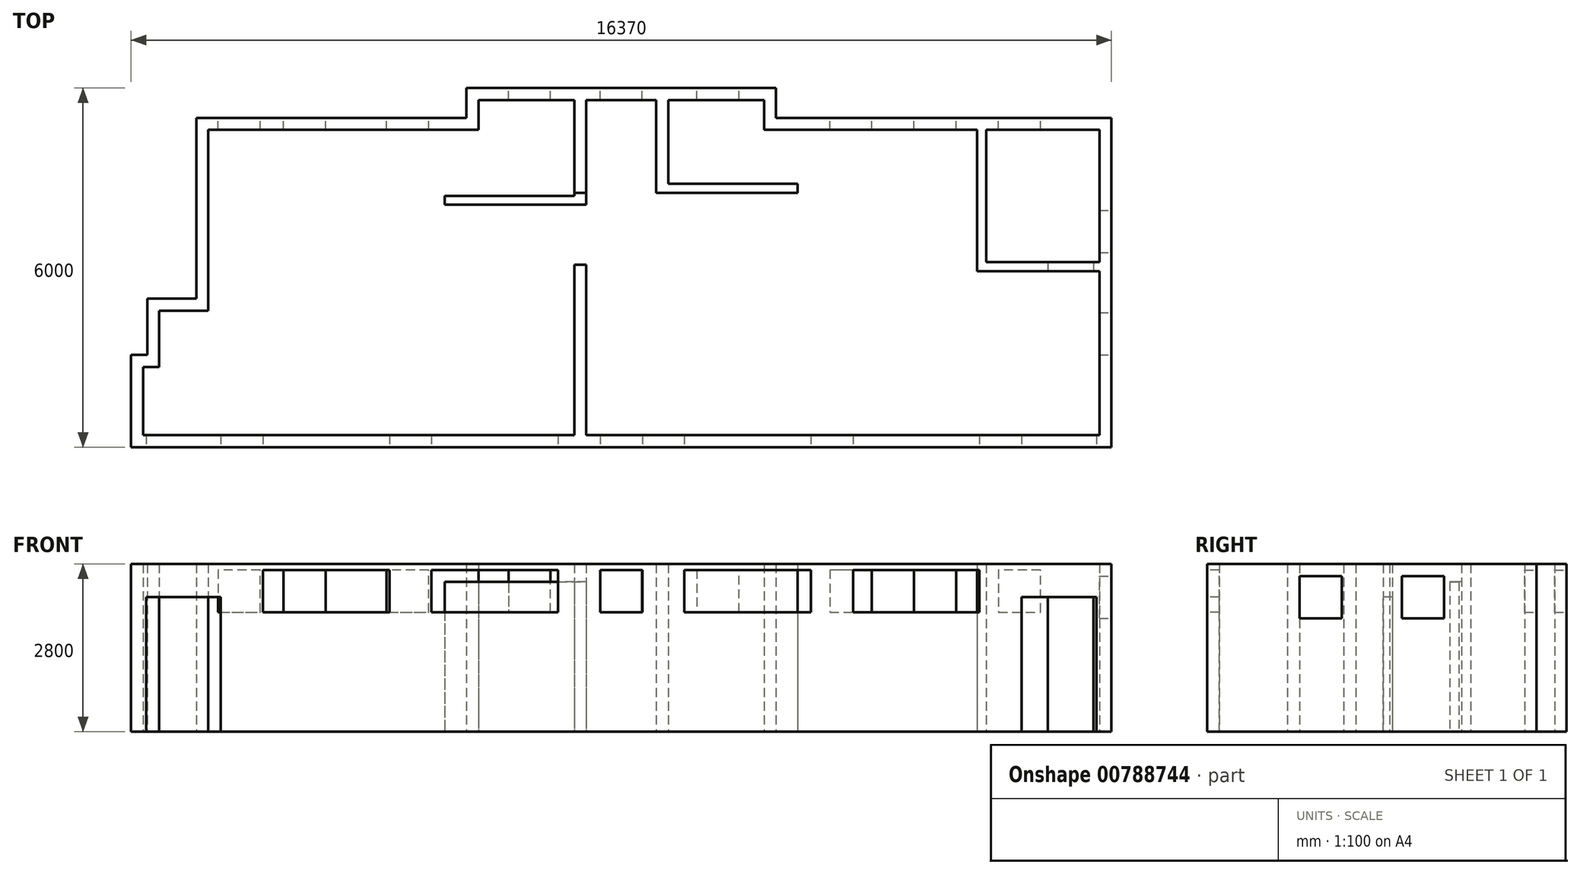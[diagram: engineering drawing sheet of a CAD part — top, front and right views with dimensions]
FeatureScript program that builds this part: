
annotation { "Feature Type Name" : "Feature", "Feature Type Description" : "" }
export const myFeature = defineFeature(function(context is Context, id is Id, definition is map)
    precondition{}
    {
        {
            var Q0;
            Q0=qCreatedBy(makeId("Top.planeOp"),FACE);
            var sketch = newSketch(context, id + "F0", { "sketchPlane" : qUnion([Q0])});
            skLineSegment(sketch, "E0", {"start": v(5800, 5300) * mm, "end": v(5800, 5800) * mm});
            skLineSegment(sketch, "E1", {"start": v(0, 0) * mm, "end": v(16370, 0) * mm});
            skLineSegment(sketch, "E2", {"start": v(16370, 0) * mm, "end": v(16370, 5500) * mm});
            skLineSegment(sketch, "E3", {"start": v(16370, 5500) * mm, "end": v(10770, 5500) * mm});
            skLineSegment(sketch, "E4", {"start": v(10770, 5500) * mm, "end": v(10770, 6000) * mm});
            skLineSegment(sketch, "E5", {"start": v(10770, 6000) * mm, "end": v(5600, 6000) * mm});
            skLineSegment(sketch, "E6", {"start": v(5600, 6000) * mm, "end": v(5600, 5500) * mm});
            skLineSegment(sketch, "E7", {"start": v(10570, 5800) * mm, "end": v(10570, 5300) * mm});
            skLineSegment(sketch, "E8", {"start": v(10570, 5300) * mm, "end": v(16170, 5300) * mm});
            skLineSegment(sketch, "E9", {"start": v(16170, 5300) * mm, "end": v(16170, 200) * mm});
            skLineSegment(sketch, "E10", {"start": v(0, 200) * mm, "end": v(0, 0) * mm});
            skLineSegment(sketch, "E11", {"start": v(0, 0) * mm, "end": v(0, 1540) * mm});
            skPoint(sketch, "E11.endSnap0", {"position": v(0, 100) * mm});
            skLineSegment(sketch, "E12", {"start": v(16170, 200) * mm, "end": v(200, 200) * mm});
            skLineSegment(sketch, "E13", {"start": v(200, 200) * mm, "end": v(200, 1340) * mm});
            skLineSegment(sketch, "E14", {"start": v(200, 1340) * mm, "end": v(470, 1340) * mm});
            skLineSegment(sketch, "E15", {"start": v(0, 1540) * mm, "end": v(270, 1540) * mm});
            skLineSegment(sketch, "E16", {"start": v(270, 1540) * mm, "end": v(270, 2480) * mm});
            skLineSegment(sketch, "E17", {"start": v(470, 1340) * mm, "end": v(470, 2280) * mm});
            skLineSegment(sketch, "E18", {"start": v(470, 2280) * mm, "end": v(936.4, 2280) * mm});
            skLineSegment(sketch, "E19", {"start": v(270, 2480) * mm, "end": v(1090, 2480) * mm});
            skLineSegment(sketch, "E20", {"start": v(5600, 5500) * mm, "end": v(1090, 5500) * mm});
            skLineSegment(sketch, "E21", {"start": v(5800, 5300) * mm, "end": v(1290, 5300) * mm});
            skLineSegment(sketch, "E22", {"start": v(1290, 5300) * mm, "end": v(1290, 2280) * mm});
            skLineSegment(sketch, "E23", {"start": v(1290, 2280) * mm, "end": v(936.4, 2280) * mm});
            skLineSegment(sketch, "E24", {"start": v(1090, 2480) * mm, "end": v(1090, 5500) * mm});
            skLineSegment(sketch, "E25", {"start": v(10570, 5800) * mm, "end": v(5800, 5800) * mm});
            skLineSegment(sketch, "E26", {"start": v(1090, 5500) * mm, "end": v(1090, 5300) * mm});
            skLineSegment(sketch, "E27", {"start": v(1090, 5500) * mm, "end": v(0, 5500) * mm});
            skLineSegment(sketch, "E28", {"start": v(0, 5500) * mm, "end": v(0, 5042) * mm});
            skLineSegment(sketch, "E29", {"start": v(0, 5042) * mm, "end": v(458, 5042) * mm});
            skLineSegment(sketch, "E30", {"start": v(458, 5042) * mm, "end": v(458, 5300) * mm});
            skLineSegment(sketch, "E31", {"start": v(458, 5300) * mm, "end": v(1090, 5300) * mm});
            skSolve(sketch);
        }
        {
            var Q0;
            {var subQ2=sQuery(id+"F0.wireOp",EDGE,"E1");Q0=makeQuery(id+"F0.imprint","IMPRINT",FACE,{"disambiguationData":[TD([[makeQuery(id+"F0.imprint","IMPRINT",EDGE,{"derivedFrom":subQ2}),1.0]])]});}
            extrude(context, id + "F1", {"entities" : qUnion([Q0]), "depth" : 2800 * mm, "offsetDistance" : 25 * mm});
        }
        {
            var Q0;
            Q0=makeQuery(id+"F1.opExtrude","SWEPT_FACE",FACE,{"disambiguationData":[OSD([sQuery(id+"F0.wireOp",EDGE,"E1")])]});
            var sketch = newSketch(context, id + "F2", { "sketchPlane" : qUnion([Q0])});
            skLineSegment(sketch, "E32", {"start": v(250, 0) * mm, "end": v(250, 2250) * mm});
            skLineSegment(sketch, "E33", {"start": v(250, 2250) * mm, "end": v(1500, 2250) * mm});
            skLineSegment(sketch, "E34", {"start": v(1500, 2250) * mm, "end": v(1500, 0) * mm});
            skLineSegment(sketch, "E35", {"start": v(1500, 0) * mm, "end": v(250, 0) * mm});
            skSolve(sketch);
        }
        {
            var Q0;
            Q0=makeQuery(id+"F2.imprint","IMPRINT",FACE,{"disambiguationData":[TD([[makeQuery(id+"F2.imprint","IMPRINT",EDGE,{"derivedFrom":sQuery(id+"F2.wireOp",EDGE,"E32")}),-1.0]])]});
            extrude(context, id + "F3", {"entities" : qUnion([Q0]), "operationType" : NewBodyOperationType.REMOVE, "oppositeDirection" : true, "depth" : 200 * mm, "offsetDistance" : 25 * mm});
        }
        {
            var Q0;
            Q0=makeQuery(id+"F1.opExtrude","SWEPT_FACE",FACE,{"disambiguationData":[OSD([sQuery(id+"F0.wireOp",EDGE,"E1")])]});
            var sketch = newSketch(context, id + "F4", { "sketchPlane" : qUnion([Q0])});
            skLineSegment(sketch, "E36", {"start": v(16120, 0) * mm, "end": v(16120, 2250) * mm});
            skLineSegment(sketch, "E37", {"start": v(16120, 2250) * mm, "end": v(14870, 2250) * mm});
            skLineSegment(sketch, "E38", {"start": v(14870, 2250) * mm, "end": v(14870, 0) * mm});
            skLineSegment(sketch, "E39", {"start": v(14870, 0) * mm, "end": v(16120, 0) * mm});
            skSolve(sketch);
        }
        {
            var Q0;
            Q0=makeQuery(id+"F4.imprint","IMPRINT",FACE,{"disambiguationData":[TD([[makeQuery(id+"F4.imprint","IMPRINT",EDGE,{"derivedFrom":sQuery(id+"F4.wireOp",EDGE,"E36")}),1.0]])]});
            extrude(context, id + "F5", {"entities" : qUnion([Q0]), "operationType" : NewBodyOperationType.REMOVE, "oppositeDirection" : true, "depth" : 200 * mm, "offsetDistance" : 25 * mm});
        }
        {
            var Q0;
            Q0=qCreatedBy(makeId("Top.planeOp"),FACE);
            var sketch = newSketch(context, id + "F6", { "sketchPlane" : qUnion([Q0])});
            skLineSegment(sketch, "E40", {"start": v(1290, 2280) * mm, "end": v(3550, 2280) * mm});
            skLineSegment(sketch, "E41", {"start": v(3550, 2280) * mm, "end": v(3550, 5300) * mm});
            skLineSegment(sketch, "E42", {"start": v(3550, 5300) * mm, "end": v(3350, 5300) * mm});
            skLineSegment(sketch, "E43", {"start": v(3350, 2480) * mm, "end": v(1290, 2480) * mm});
            skLineSegment(sketch, "E44", {"start": v(1290, 2480) * mm, "end": v(1290, 2280) * mm});
            skLineSegment(sketch, "E45", {"start": v(3350, 5300) * mm, "end": v(3350, 2480) * mm});
            skSolve(sketch);
        }
        {
            var Q0;
            Q0=qCreatedBy(makeId("Top.planeOp"),FACE);
            var sketch = newSketch(context, id + "F7", { "sketchPlane" : qUnion([Q0])});
            skLineSegment(sketch, "E46.0", {"start": v(5800, 5300) * mm, "end": v(5800, 5800) * mm});
            skLineSegment(sketch, "E47.0", {"start": v(10570, 5800) * mm, "end": v(5800, 5800) * mm});
            skLineSegment(sketch, "E48.0", {"start": v(16170, 200) * mm, "end": v(200, 200) * mm});
            skLineSegment(sketch, "E49", {"start": v(5800, 5800) * mm, "end": v(7400, 5800) * mm});
            skLineSegment(sketch, "E50", {"start": v(7400, 5800) * mm, "end": v(7600, 5800) * mm});
            skLineSegment(sketch, "E51", {"start": v(7600, 5800) * mm, "end": v(7600, 200) * mm});
            skLineSegment(sketch, "E52", {"start": v(7400, 5800) * mm, "end": v(7400, 200) * mm});
            skSolve(sketch);
        }
        {
            var Q0;
            Q0=qCreatedBy(makeId("Top.planeOp"),FACE);
            var sketch = newSketch(context, id + "F8", { "sketchPlane" : qUnion([Q0])});
            skLineSegment(sketch, "E53.0", {"start": v(10570, 5800) * mm, "end": v(10570, 5300) * mm});
            skLineSegment(sketch, "E53.1", {"start": v(10570, 5800) * mm, "end": v(5800, 5800) * mm});
            skLineSegment(sketch, "E53.2", {"start": v(16170, 200) * mm, "end": v(200, 200) * mm});
            skLineSegment(sketch, "E54", {"start": v(8970, 200) * mm, "end": v(8770, 200) * mm});
            skLineSegment(sketch, "E55", {"start": v(8770, 200) * mm, "end": v(8770, 5800) * mm});
            skLineSegment(sketch, "E56", {"start": v(8770, 5800) * mm, "end": v(8970, 5800) * mm});
            skLineSegment(sketch, "E57", {"start": v(8970, 5800) * mm, "end": v(8970, 200) * mm});
            skSolve(sketch);
        }
        {
            var Q0;
            Q0=qCreatedBy(makeId("Top.planeOp"),FACE);
            var sketch = newSketch(context, id + "F9", { "sketchPlane" : qUnion([Q0])});
            skLineSegment(sketch, "E58.0", {"start": v(10570, 5800) * mm, "end": v(5800, 5800) * mm});
            skLineSegment(sketch, "E58.1", {"start": v(10570, 5800) * mm, "end": v(10570, 5300) * mm});
            skLineSegment(sketch, "E59", {"start": v(10570, 5800) * mm, "end": v(8969, 5800) * mm});
            skLineSegment(sketch, "E60", {"start": v(8969, 5800) * mm, "end": v(8969, 4400) * mm});
            skLineSegment(sketch, "E61", {"start": v(8969, 4400) * mm, "end": v(11129, 4400) * mm});
            skLineSegment(sketch, "E62", {"start": v(11129, 4400) * mm, "end": v(11129, 4250) * mm});
            skLineSegment(sketch, "E63", {"start": v(11129, 4250) * mm, "end": v(8769, 4250) * mm});
            skLineSegment(sketch, "E64", {"start": v(8769, 4250) * mm, "end": v(8769, 5800) * mm});
            skSolve(sketch);
        }
        {
            var Q0;
            Q0=qCreatedBy(makeId("Top.planeOp"),FACE);
            var sketch = newSketch(context, id + "F10", { "sketchPlane" : qUnion([Q0])});
            skLineSegment(sketch, "E65", {"start": v(7400, 5800) * mm, "end": v(7400, 4200) * mm});
            skLineSegment(sketch, "E66", {"start": v(7400, 4200) * mm, "end": v(5240, 4200) * mm});
            skLineSegment(sketch, "E67", {"start": v(5240, 4200) * mm, "end": v(5240, 4050) * mm});
            skLineSegment(sketch, "E68", {"start": v(5240, 4050) * mm, "end": v(7600, 4050) * mm});
            skLineSegment(sketch, "E69", {"start": v(7600, 4050) * mm, "end": v(7600, 5800) * mm});
            skLineSegment(sketch, "E70", {"start": v(7400, 5800) * mm, "end": v(7600, 5800) * mm});
            skSolve(sketch);
        }
        {
            var Q0;
            Q0=qSketchRegion(id+"F10",true);
            extrude(context, id + "F11", {"entities" : qUnion([Q0]), "operationType" : NewBodyOperationType.ADD, "depth" : 2500 * mm, "offsetDistance" : 25 * mm});
        }
        {
            var Q0;
            Q0=qCreatedBy(makeId("Top.planeOp"),FACE);
            var sketch = newSketch(context, id + "F12", { "sketchPlane" : qUnion([Q0])});
            skLineSegment(sketch, "E71.0", {"start": v(10570, 5300) * mm, "end": v(16170, 5300) * mm});
            skLineSegment(sketch, "E71.1", {"start": v(16170, 5300) * mm, "end": v(16170, 200) * mm});
            skLineSegment(sketch, "E72", {"start": v(16170, 5300) * mm, "end": v(16170, 3090) * mm});
            skLineSegment(sketch, "E73", {"start": v(16170, 3090) * mm, "end": v(14280, 3090) * mm});
            skLineSegment(sketch, "E74", {"start": v(14280, 3090) * mm, "end": v(14280, 5300) * mm});
            skLineSegment(sketch, "E75", {"start": v(14280, 5300) * mm, "end": v(14130, 5300) * mm});
            skLineSegment(sketch, "E76", {"start": v(14130, 5300) * mm, "end": v(14130, 2940) * mm});
            skLineSegment(sketch, "E77", {"start": v(14130, 2940) * mm, "end": v(16170, 2940) * mm});
            skSolve(sketch);
        }
        {
            var Q0;
            {var subQ0=sQuery(id+"F12.wireOp",EDGE,"E73");Q0=makeQuery(id+"F12.imprint","IMPRINT",FACE,{"disambiguationData":[TD([[makeQuery(id+"F12.imprint","IMPRINT",EDGE,{"derivedFrom":subQ0}),1.0]])]});}
            extrude(context, id + "F13", {"entities" : qUnion([Q0]), "operationType" : NewBodyOperationType.ADD, "depth" : 2800 * mm, "offsetDistance" : 25 * mm});
        }
        {
            var Q0;
            Q0=makeQuery(id+"F1.opExtrude","SWEPT_FACE",FACE,{"disambiguationData":[OSD([sQuery(id+"F0.wireOp",EDGE,"E1")])]});
            var sketch = newSketch(context, id + "F14", { "sketchPlane" : qUnion([Q0])});
            skLineSegment(sketch, "E78", {"start": v(2204, 1996) * mm, "end": v(2204, 2700) * mm});
            skLineSegment(sketch, "E79", {"start": v(2204, 2700) * mm, "end": v(4315, 2700) * mm});
            skLineSegment(sketch, "E80", {"start": v(4315, 2700) * mm, "end": v(4315, 1996) * mm});
            skLineSegment(sketch, "E81", {"start": v(4315, 1996) * mm, "end": v(2204, 1996) * mm});
            skLineSegment(sketch, "E82", {"start": v(5018, 1996) * mm, "end": v(5018, 2700) * mm});
            skLineSegment(sketch, "E83", {"start": v(5018, 2700) * mm, "end": v(7129, 2700) * mm});
            skLineSegment(sketch, "E84", {"start": v(7129, 2700) * mm, "end": v(7129, 1996) * mm});
            skLineSegment(sketch, "E85", {"start": v(7129, 1996) * mm, "end": v(5018, 1996) * mm});
            skLineSegment(sketch, "E86", {"start": v(7833, 1996) * mm, "end": v(7833, 2700) * mm});
            skLineSegment(sketch, "E87", {"start": v(7833, 2700) * mm, "end": v(8537, 2700) * mm});
            skLineSegment(sketch, "E88", {"start": v(8537, 2700) * mm, "end": v(8537, 1996) * mm});
            skLineSegment(sketch, "E89", {"start": v(8537, 1996) * mm, "end": v(7833, 1996) * mm});
            skLineSegment(sketch, "E90", {"start": v(9241, 1996) * mm, "end": v(9241, 2700) * mm});
            skLineSegment(sketch, "E91", {"start": v(9241, 2700) * mm, "end": v(11352, 2700) * mm});
            skLineSegment(sketch, "E92", {"start": v(11352, 2700) * mm, "end": v(11352, 1996) * mm});
            skLineSegment(sketch, "E93", {"start": v(11352, 1996) * mm, "end": v(9241, 1996) * mm});
            skLineSegment(sketch, "E94", {"start": v(12056, 1996) * mm, "end": v(12056, 2700) * mm});
            skLineSegment(sketch, "E95", {"start": v(12056, 2700) * mm, "end": v(14167, 2700) * mm});
            skLineSegment(sketch, "E96", {"start": v(14167, 2700) * mm, "end": v(14167, 1996) * mm});
            skLineSegment(sketch, "E97", {"start": v(14167, 1996) * mm, "end": v(12056, 1996) * mm});
            skSolve(sketch);
        }
        {
            var Q0;
            Q0=makeQuery(id+"F14.imprint","IMPRINT",FACE,{"disambiguationData":[TD([[makeQuery(id+"F14.imprint","IMPRINT",EDGE,{"derivedFrom":sQuery(id+"F14.wireOp",EDGE,"E78")}),-1.0]])]});
            var Q1;
            Q1=makeQuery(id+"F14.imprint","IMPRINT",FACE,{"disambiguationData":[TD([[makeQuery(id+"F14.imprint","IMPRINT",EDGE,{"derivedFrom":sQuery(id+"F14.wireOp",EDGE,"E82")}),-1.0]])]});
            var Q2;
            Q2=makeQuery(id+"F14.imprint","IMPRINT",FACE,{"disambiguationData":[TD([[makeQuery(id+"F14.imprint","IMPRINT",EDGE,{"derivedFrom":sQuery(id+"F14.wireOp",EDGE,"E86")}),-1.0]])]});
            var Q3;
            Q3=makeQuery(id+"F14.imprint","IMPRINT",FACE,{"disambiguationData":[TD([[makeQuery(id+"F14.imprint","IMPRINT",EDGE,{"derivedFrom":sQuery(id+"F14.wireOp",EDGE,"E90")}),-1.0]])]});
            var Q4;
            Q4=makeQuery(id+"F14.imprint","IMPRINT",FACE,{"disambiguationData":[TD([[makeQuery(id+"F14.imprint","IMPRINT",EDGE,{"derivedFrom":sQuery(id+"F14.wireOp",EDGE,"E94")}),-1.0]])]});
            extrude(context, id + "F15", {"entities" : qUnion([Q0, Q1, Q2, Q3, Q4]), "operationType" : NewBodyOperationType.REMOVE, "oppositeDirection" : true, "depth" : 200 * mm, "offsetDistance" : 25 * mm});
        }
        {
            var Q0;
            Q0=makeQuery(id+"F1.opExtrude","SWEPT_FACE",FACE,{"disambiguationData":[OSD([sQuery(id+"F0.wireOp",EDGE,"E3")])]});
            var sketch = newSketch(context, id + "F16", { "sketchPlane" : qUnion([Q0])});
            skLineSegment(sketch, "E98", {"start": v(-15187, 1996) * mm, "end": v(-15187, 2700) * mm});
            skLineSegment(sketch, "E99", {"start": v(-15187, 2700) * mm, "end": v(-14483, 2700) * mm});
            skLineSegment(sketch, "E100", {"start": v(-14483, 2700) * mm, "end": v(-14483, 1996) * mm});
            skLineSegment(sketch, "E101", {"start": v(-14483, 1996) * mm, "end": v(-15187, 1996) * mm});
            skLineSegment(sketch, "E102", {"start": v(-13779, 1996) * mm, "end": v(-13779, 2700) * mm});
            skLineSegment(sketch, "E103", {"start": v(-13779, 2700) * mm, "end": v(-13075, 2700) * mm});
            skLineSegment(sketch, "E104", {"start": v(-13075, 2700) * mm, "end": v(-13075, 1996) * mm});
            skLineSegment(sketch, "E105", {"start": v(-13075, 1996) * mm, "end": v(-13779, 1996) * mm});
            skLineSegment(sketch, "E106", {"start": v(-12371, 1996) * mm, "end": v(-12371, 2700) * mm});
            skLineSegment(sketch, "E107", {"start": v(-12371, 2700) * mm, "end": v(-11667, 2700) * mm});
            skLineSegment(sketch, "E108", {"start": v(-11667, 2700) * mm, "end": v(-11667, 1996) * mm});
            skLineSegment(sketch, "E109", {"start": v(-11667, 1996) * mm, "end": v(-12371, 1996) * mm});
            skSolve(sketch);
        }
        {
            var Q0;
            Q0=makeQuery(id+"F16.imprint","IMPRINT",FACE,{"disambiguationData":[TD([[makeQuery(id+"F16.imprint","IMPRINT",EDGE,{"derivedFrom":sQuery(id+"F16.wireOp",EDGE,"E98")}),-1.0]])]});
            var Q1;
            Q1=makeQuery(id+"F16.imprint","IMPRINT",FACE,{"disambiguationData":[TD([[makeQuery(id+"F16.imprint","IMPRINT",EDGE,{"derivedFrom":sQuery(id+"F16.wireOp",EDGE,"E102")}),-1.0]])]});
            var Q2;
            Q2=makeQuery(id+"F16.imprint","IMPRINT",FACE,{"disambiguationData":[TD([[makeQuery(id+"F16.imprint","IMPRINT",EDGE,{"derivedFrom":sQuery(id+"F16.wireOp",EDGE,"E106")}),-1.0]])]});
            extrude(context, id + "F17", {"entities" : qUnion([Q0, Q1, Q2]), "operationType" : NewBodyOperationType.REMOVE, "oppositeDirection" : true, "depth" : 200 * mm, "offsetDistance" : 25 * mm});
        }
        {
            var Q0;
            Q0=makeQuery(id+"F1.opExtrude","SWEPT_FACE",FACE,{"disambiguationData":[OSD([sQuery(id+"F0.wireOp",EDGE,"E5")])]});
            var sketch = newSketch(context, id + "F18", { "sketchPlane" : qUnion([Q0])});
            skLineSegment(sketch, "E110", {"start": v(-10150, 1996) * mm, "end": v(-10150, 2700) * mm});
            skLineSegment(sketch, "E111", {"start": v(-10150, 2700) * mm, "end": v(-9446, 2700) * mm});
            skLineSegment(sketch, "E112", {"start": v(-9446, 2700) * mm, "end": v(-9446, 1996) * mm});
            skLineSegment(sketch, "E113", {"start": v(-9446, 1996) * mm, "end": v(-10150, 1996) * mm});
            skLineSegment(sketch, "E114", {"start": v(-8536, 1996) * mm, "end": v(-8536, 2700) * mm});
            skLineSegment(sketch, "E115", {"start": v(-8536, 2700) * mm, "end": v(-7832, 2700) * mm});
            skLineSegment(sketch, "E116", {"start": v(-7832, 2700) * mm, "end": v(-7832, 1996) * mm});
            skLineSegment(sketch, "E117", {"start": v(-7832, 1996) * mm, "end": v(-8536, 1996) * mm});
            skLineSegment(sketch, "E118", {"start": v(-7005, 1996) * mm, "end": v(-7005, 2700) * mm});
            skLineSegment(sketch, "E119", {"start": v(-7005, 2700) * mm, "end": v(-6301, 2700) * mm});
            skLineSegment(sketch, "E120", {"start": v(-6301, 2700) * mm, "end": v(-6301, 1996) * mm});
            skLineSegment(sketch, "E121", {"start": v(-6301, 1996) * mm, "end": v(-7005, 1996) * mm});
            skSolve(sketch);
        }
        {
            var Q0;
            Q0=makeQuery(id+"F18.imprint","IMPRINT",FACE,{"disambiguationData":[TD([[makeQuery(id+"F18.imprint","IMPRINT",EDGE,{"derivedFrom":sQuery(id+"F18.wireOp",EDGE,"E110")}),-1.0]])]});
            var Q1;
            Q1=makeQuery(id+"F18.imprint","IMPRINT",FACE,{"disambiguationData":[TD([[makeQuery(id+"F18.imprint","IMPRINT",EDGE,{"derivedFrom":sQuery(id+"F18.wireOp",EDGE,"E114")}),-1.0]])]});
            var Q2;
            Q2=makeQuery(id+"F18.imprint","IMPRINT",FACE,{"disambiguationData":[TD([[makeQuery(id+"F18.imprint","IMPRINT",EDGE,{"derivedFrom":sQuery(id+"F18.wireOp",EDGE,"E118")}),-1.0]])]});
            extrude(context, id + "F19", {"entities" : qUnion([Q0, Q1, Q2]), "operationType" : NewBodyOperationType.REMOVE, "oppositeDirection" : true, "depth" : 200 * mm, "offsetDistance" : 25 * mm});
        }
        {
            var Q0;
            Q0=makeQuery(id+"F1.opExtrude","SWEPT_FACE",FACE,{"disambiguationData":[OSD([sQuery(id+"F0.wireOp",EDGE,"E20")])]});
            var sketch = newSketch(context, id + "F20", { "sketchPlane" : qUnion([Q0])});
            skLineSegment(sketch, "E122", {"start": v(-4969, 1996) * mm, "end": v(-4969, 2700) * mm});
            skLineSegment(sketch, "E123", {"start": v(-4969, 2700) * mm, "end": v(-4265, 2700) * mm});
            skLineSegment(sketch, "E124", {"start": v(-4265, 2700) * mm, "end": v(-4265, 1996) * mm});
            skLineSegment(sketch, "E125", {"start": v(-4265, 1996) * mm, "end": v(-4969, 1996) * mm});
            skLineSegment(sketch, "E126", {"start": v(-3248, 1996) * mm, "end": v(-3248, 2700) * mm});
            skLineSegment(sketch, "E127", {"start": v(-3248, 2700) * mm, "end": v(-2544, 2700) * mm});
            skLineSegment(sketch, "E128", {"start": v(-2544, 2700) * mm, "end": v(-2544, 1996) * mm});
            skLineSegment(sketch, "E129", {"start": v(-2544, 1996) * mm, "end": v(-3248, 1996) * mm});
            skLineSegment(sketch, "E130", {"start": v(-2156, 1996) * mm, "end": v(-2156, 2700) * mm});
            skLineSegment(sketch, "E131", {"start": v(-2156, 2700) * mm, "end": v(-1452, 2700) * mm});
            skLineSegment(sketch, "E132", {"start": v(-1452, 2700) * mm, "end": v(-1452, 1996) * mm});
            skLineSegment(sketch, "E133", {"start": v(-1452, 1996) * mm, "end": v(-2156, 1996) * mm});
            skSolve(sketch);
        }
        {
            var Q0;
            Q0=makeQuery(id+"F20.imprint","IMPRINT",FACE,{"disambiguationData":[TD([[makeQuery(id+"F20.imprint","IMPRINT",EDGE,{"derivedFrom":sQuery(id+"F20.wireOp",EDGE,"E122")}),-1.0]])]});
            var Q1;
            Q1=makeQuery(id+"F20.imprint","IMPRINT",FACE,{"disambiguationData":[TD([[makeQuery(id+"F20.imprint","IMPRINT",EDGE,{"derivedFrom":sQuery(id+"F20.wireOp",EDGE,"E126")}),-1.0]])]});
            var Q2;
            Q2=makeQuery(id+"F20.imprint","IMPRINT",FACE,{"disambiguationData":[TD([[makeQuery(id+"F20.imprint","IMPRINT",EDGE,{"derivedFrom":sQuery(id+"F20.wireOp",EDGE,"E130")}),-1.0]])]});
            extrude(context, id + "F21", {"entities" : qUnion([Q0, Q1, Q2]), "operationType" : NewBodyOperationType.REMOVE, "oppositeDirection" : true, "depth" : 200 * mm, "offsetDistance" : 25 * mm});
        }
        {
            var Q0;
            Q0=qCreatedBy(makeId("Top.planeOp"),FACE);
            var sketch = newSketch(context, id + "F22", { "sketchPlane" : qUnion([Q0])});
            skLineSegment(sketch, "E134.0", {"start": v(10570, 5800) * mm, "end": v(10570, 5300) * mm});
            skLineSegment(sketch, "E134.1", {"start": v(10570, 5800) * mm, "end": v(5800, 5800) * mm});
            skLineSegment(sketch, "E135", {"start": v(10570, 5300) * mm, "end": v(10570, 4300) * mm});
            skLineSegment(sketch, "E136", {"start": v(7750, 5800) * mm, "end": v(7600, 5800) * mm});
            skLineSegment(sketch, "E137", {"start": v(10720, 4150) * mm, "end": v(10720, 5300) * mm});
            skLineSegment(sketch, "E138", {"start": v(10720, 5300) * mm, "end": v(10570, 5300) * mm});
            skLineSegment(sketch, "E139.0", {"start": v(7400, 5800) * mm, "end": v(7400, 200) * mm});
            skLineSegment(sketch, "E140", {"start": v(10570, 4300) * mm, "end": v(7600, 4300) * mm});
            skLineSegment(sketch, "E141", {"start": v(7600, 4150) * mm, "end": v(10720, 4150) * mm});
            skLineSegment(sketch, "E142", {"start": v(7600, 4150) * mm, "end": v(7400, 4150) * mm});
            skLineSegment(sketch, "E143", {"start": v(7400, 4150) * mm, "end": v(7400, 5800) * mm});
            skLineSegment(sketch, "E144", {"start": v(7400, 5800) * mm, "end": v(7600, 5800) * mm});
            skLineSegment(sketch, "E145", {"start": v(7600, 5800) * mm, "end": v(7600, 4300) * mm});
            skSolve(sketch);
        }
        {
            var Q0;
            Q0=qCreatedBy(makeId("Top.planeOp"),FACE);
            var sketch = newSketch(context, id + "F23", { "sketchPlane" : qUnion([Q0])});
            skLineSegment(sketch, "E146.0", {"start": v(10720, 4150) * mm, "end": v(10720, 4150) * mm});
            skLineSegment(sketch, "E147", {"start": v(8970, 2650) * mm, "end": v(9720, 2650) * mm});
            skLineSegment(sketch, "E148", {"start": v(8770, 2650) * mm, "end": v(8770, 4300) * mm});
            skLineSegment(sketch, "E149", {"start": v(8770, 4300) * mm, "end": v(8970, 4300) * mm});
            skLineSegment(sketch, "E150", {"start": v(8970, 4300) * mm, "end": v(8970, 2650) * mm});
            skLineSegment(sketch, "E151", {"start": v(8970, 2500) * mm, "end": v(9720, 2500) * mm});
            skLineSegment(sketch, "E152", {"start": v(9720, 2500) * mm, "end": v(9720, 2650) * mm});
            skLineSegment(sketch, "E153", {"start": v(8970, 2500) * mm, "end": v(8970, 1200) * mm});
            skLineSegment(sketch, "E154", {"start": v(8970, 1200) * mm, "end": v(8770, 1200) * mm});
            skLineSegment(sketch, "E155", {"start": v(8770, 1200) * mm, "end": v(8770, 2650) * mm});
            skSolve(sketch);
        }
        {
            var Q0;
            Q0=qCreatedBy(makeId("Top.planeOp"),FACE);
            var sketch = newSketch(context, id + "F24", { "sketchPlane" : qUnion([Q0])});
            skLineSegment(sketch, "E156.0", {"start": v(7400, 5800) * mm, "end": v(7400, 200) * mm});
            skLineSegment(sketch, "E156.1", {"start": v(10570, 5800) * mm, "end": v(5800, 5800) * mm});
            skLineSegment(sketch, "E156.2", {"start": v(7600, 5800) * mm, "end": v(7600, 200) * mm});
            skLineSegment(sketch, "E157", {"start": v(7400, 5800) * mm, "end": v(7600, 5800) * mm});
            skLineSegment(sketch, "E158", {"start": v(7600, 5800) * mm, "end": v(7600, 1200) * mm});
            skLineSegment(sketch, "E159", {"start": v(7600, 1200) * mm, "end": v(7400, 1200) * mm});
            skLineSegment(sketch, "E160", {"start": v(7400, 1200) * mm, "end": v(7400, 5800) * mm});
            skSolve(sketch);
        }
        {
            var Q0;
            Q0=makeQuery(id+"FZt5gqYlXnzUQJP_1.opExtrude","SWEPT_FACE",FACE,{"disambiguationData":[OSD([sQuery(id+"F7.wireOp",EDGE,"E51")])]});
            var sketch = newSketch(context, id + "F25", { "sketchPlane" : qUnion([Q0])});
            skLineSegment(sketch, "E161.0", {"start": v(5800, 2800) * mm, "end": v(5800, 0) * mm});
            skLineSegment(sketch, "E162.0", {"start": v(4250, 0) * mm, "end": v(5800, 0) * mm});
            skLineSegment(sketch, "E163", {"start": v(5800, 0) * mm, "end": v(3600, 0) * mm});
            skLineSegment(sketch, "E164", {"start": v(3600, 0) * mm, "end": v(3600, 2100) * mm});
            skLineSegment(sketch, "E165", {"start": v(3600, 2100) * mm, "end": v(2400, 2100) * mm});
            skLineSegment(sketch, "E166", {"start": v(2400, 2100) * mm, "end": v(2400, 0) * mm});
            skLineSegment(sketch, "E167", {"start": v(2400, 0) * mm, "end": v(3600, 0) * mm});
            skSolve(sketch);
        }
        {
            var Q0;
            {var subQ0=sQuery(id+"F10.wireOp",EDGE,"E66");Q0=makeQuery(id+"FqNkP1vWDE5f3xF_1.boolean.opBoolean","MERGE",FACE,{"derivedFrom":[makeQuery(id+"F11.opExtrude","SWEPT_FACE",FACE,{"disambiguationData":[OSD([subQ0])]}),makeQuery(id+"FqNkP1vWDE5f3xF_1.opExtrude","SWEPT_FACE",FACE,{"disambiguationData":[OSD([subQ0])]})]});}
            var sketch = newSketch(context, id + "F26", { "sketchPlane" : qUnion([Q0])});
            skLineSegment(sketch, "E168", {"start": v(-5240, 2800) * mm, "end": v(-5240, 2450) * mm});
            skLineSegment(sketch, "E169", {"start": v(-5240, 2450) * mm, "end": v(-5390, 2450) * mm});
            skLineSegment(sketch, "E170", {"start": v(-5390, 2450) * mm, "end": v(-5390, 2800) * mm});
            skLineSegment(sketch, "E171", {"start": v(-5390, 2800) * mm, "end": v(-5240, 2800) * mm});
            skSolve(sketch);
        }
        {
            var Q0;
            Q0=makeQuery(id+"F13.opExtrude","SWEPT_FACE",FACE,{"disambiguationData":[OSD([sQuery(id+"F12.wireOp",EDGE,"E77")])]});
            var sketch = newSketch(context, id + "F27", { "sketchPlane" : qUnion([Q0])});
            skLineSegment(sketch, "E172.0", {"start": v(16170, 2800) * mm, "end": v(16170, 0) * mm});
            skLineSegment(sketch, "E173", {"start": v(16170, 0) * mm, "end": v(16070, 0) * mm});
            skLineSegment(sketch, "E174", {"start": v(16070, 0) * mm, "end": v(16070, 2250) * mm});
            skLineSegment(sketch, "E175", {"start": v(16070, 2250) * mm, "end": v(15310, 2250) * mm});
            skLineSegment(sketch, "E176", {"start": v(15310, 2250) * mm, "end": v(15310, 0) * mm});
            skLineSegment(sketch, "E177", {"start": v(15310, 0) * mm, "end": v(16070, 0) * mm});
            skSolve(sketch);
        }
        {
            var Q0;
            Q0=qSketchRegion(id+"F27",true);
            extrude(context, id + "F28", {"entities" : qUnion([Q0]), "operationType" : NewBodyOperationType.REMOVE, "oppositeDirection" : true, "depth" : 150 * mm, "offsetDistance" : 25 * mm});
        }
        {
            var Q0;
            Q0=makeQuery(id+"F1.opExtrude","SWEPT_FACE",FACE,{"disambiguationData":[OSD([sQuery(id+"F0.wireOp",EDGE,"E2")])]});
            var sketch = newSketch(context, id + "F29", { "sketchPlane" : qUnion([Q0])});
            skLineSegment(sketch, "E178.0", {"start": v(0, 2800) * mm, "end": v(0, 0) * mm});
            skLineSegment(sketch, "E179", {"start": v(1545, 2600) * mm, "end": v(1545, 1895) * mm});
            skLineSegment(sketch, "E180", {"start": v(1545, 1895) * mm, "end": v(2250, 1895) * mm});
            skLineSegment(sketch, "E181", {"start": v(2250, 1895) * mm, "end": v(2250, 2600) * mm});
            skLineSegment(sketch, "E182", {"start": v(2250, 2600) * mm, "end": v(1545, 2600) * mm});
            skLineSegment(sketch, "E183", {"start": v(3250, 2600) * mm, "end": v(3250, 1895) * mm});
            skLineSegment(sketch, "E184", {"start": v(3250, 1895) * mm, "end": v(3955, 1895) * mm});
            skLineSegment(sketch, "E185", {"start": v(3955, 1895) * mm, "end": v(3955, 2600) * mm});
            skLineSegment(sketch, "E186", {"start": v(3955, 2600) * mm, "end": v(3250, 2600) * mm});
            skSolve(sketch);
        }
        {
            var Q0;
            Q0=makeQuery(id+"F29.imprint","IMPRINT",FACE,{"disambiguationData":[TD([[makeQuery(id+"F29.imprint","IMPRINT",EDGE,{"derivedFrom":sQuery(id+"F29.wireOp",EDGE,"E179")}),1.0]])]});
            var Q1;
            Q1=makeQuery(id+"F29.imprint","IMPRINT",FACE,{"disambiguationData":[TD([[makeQuery(id+"F29.imprint","IMPRINT",EDGE,{"derivedFrom":sQuery(id+"F29.wireOp",EDGE,"E183")}),1.0]])]});
            extrude(context, id + "F30", {"entities" : qUnion([Q0, Q1]), "operationType" : NewBodyOperationType.REMOVE, "oppositeDirection" : true, "depth" : 200 * mm, "offsetDistance" : 25 * mm});
        }
        {
            var Q0;
            {var subQ0=sQuery(id+"F26.wireOp",EDGE,"E171");var subQ1=sQuery(id+"F10.wireOp",EDGE,"E68");Q0=makeQuery(id+"FKpUyMkFG7JmVFU_1.boolean.opBoolean","MERGE",FACE,{"derivedFrom":[makeQuery(id+"F33t2RGtVH02w4j_1.boolean.opBoolean","MERGE",FACE,{"derivedFrom":[makeQuery(id+"FqNkP1vWDE5f3xF_1.boolean.opBoolean","MERGE",FACE,{"derivedFrom":[makeQuery(id+"FZt5gqYlXnzUQJP_1.boolean.opBoolean","MERGE",FACE,{"derivedFrom":[makeQuery(id+"F1.opExtrude","CAP_FACE",FACE,{"disambiguationData":[OSD([sQuery(id+"F0.wireOp",EDGE,"E1"),sQuery(id+"F0.wireOp",EDGE,"E2"),sQuery(id+"F0.wireOp",EDGE,"E3"),sQuery(id+"F0.wireOp",EDGE,"E4"),sQuery(id+"F0.wireOp",EDGE,"E5"),sQuery(id+"F0.wireOp",EDGE,"E6"),sQuery(id+"F0.wireOp",EDGE,"E0"),sQuery(id+"F0.wireOp",EDGE,"E7"),sQuery(id+"F0.wireOp",EDGE,"E8"),sQuery(id+"F0.wireOp",EDGE,"E9"),sQuery(id+"F0.wireOp",EDGE,"E11"),sQuery(id+"F0.wireOp",EDGE,"E12"),sQuery(id+"F0.wireOp",EDGE,"E13"),sQuery(id+"F0.wireOp",EDGE,"E14"),sQuery(id+"F0.wireOp",EDGE,"E15"),sQuery(id+"F0.wireOp",EDGE,"E16"),sQuery(id+"F0.wireOp",EDGE,"E17"),sQuery(id+"F0.wireOp",EDGE,"E18"),sQuery(id+"F0.wireOp",EDGE,"E19"),sQuery(id+"F0.wireOp",EDGE,"E20"),sQuery(id+"F0.wireOp",EDGE,"E21"),sQuery(id+"F0.wireOp",EDGE,"E22"),sQuery(id+"F0.wireOp",EDGE,"E23"),sQuery(id+"F0.wireOp",EDGE,"E24"),sQuery(id+"F0.wireOp",EDGE,"E25"),sQuery(id+"F0.wireOp",EDGE,"E26")])],"isStart":false}),makeQuery(id+"FZt5gqYlXnzUQJP_1.opExtrude","CAP_FACE",FACE,{"disambiguationData":[OSD([sQuery(id+"F7.wireOp",EDGE,"E48.0"),sQuery(id+"F7.wireOp",EDGE,"E50"),sQuery(id+"F7.wireOp",EDGE,"E51"),sQuery(id+"F7.wireOp",EDGE,"E52")])],"isStart":false})]}),makeQuery(id+"FqNkP1vWDE5f3xF_1.opExtrude","CAP_FACE",FACE,{"disambiguationData":[OSD([sQuery(id+"F10.wireOp",EDGE,"E65"),sQuery(id+"F10.wireOp",EDGE,"E66"),sQuery(id+"F10.wireOp",EDGE,"E67"),subQ1,sQuery(id+"F10.wireOp",EDGE,"E69"),sQuery(id+"F10.wireOp",EDGE,"E70")])],"isStart":false})]}),makeQuery(id+"F33t2RGtVH02w4j_1.opExtrude","SWEPT_FACE",FACE,{"disambiguationData":[OSD([subQ0])]})]}),makeQuery(id+"FKpUyMkFG7JmVFU_1.opExtrude","SWEPT_FACE",FACE,{"disambiguationData":[OSD([subQ1]),TDD([makeQuery(id+"FqNkP1vWDE5f3xF_1.opExtrude","CAP_EDGE",EDGE,{"disambiguationData":[OSD([subQ1])],"isStart":false})])]}),makeQuery(id+"FKpUyMkFG7JmVFU_1.opExtrude","SWEPT_FACE",FACE,{"disambiguationData":[OSD([subQ0])]})]});}
            var sketch = newSketch(context, id + "F31", { "sketchPlane" : qUnion([Q0])});
            skLineSegment(sketch, "E187.0", {"start": v(5240, 4050) * mm, "end": v(7600, 4050) * mm});
            skLineSegment(sketch, "E188", {"start": v(5240, 4050) * mm, "end": v(5290, 4050) * mm});
            skLineSegment(sketch, "E189", {"start": v(5290, 4050) * mm, "end": v(5293, 4050) * mm});
            skLineSegment(sketch, "E190", {"start": v(5293, 4050) * mm, "end": v(5293, 2050) * mm});
            skLineSegment(sketch, "E191", {"start": v(5293, 2050) * mm, "end": v(5290.5, 2050) * mm});
            skLineSegment(sketch, "E192", {"start": v(5290.5, 2050) * mm, "end": v(5290, 4050) * mm});
            skSolve(sketch);
        }
        {
            var Q0;
            Q0=qSketchRegion(id+"F9",true);
            extrude(context, id + "F32", {"entities" : qUnion([Q0]), "operationType" : NewBodyOperationType.ADD, "depth" : 2800 * mm, "offsetDistance" : 25 * mm});
        }
        {
            var Q0;
            Q0=qCreatedBy(makeId("Top.planeOp"),FACE);
            var sketch = newSketch(context, id + "F33", { "sketchPlane" : qUnion([Q0])});
            skLineSegment(sketch, "E193.0.0", {"start": v(7600, 5800) * mm, "end": v(7400, 5800) * mm});
            skLineSegment(sketch, "E193.0.1", {"start": v(7400, 5800) * mm, "end": v(7400, 200) * mm});
            skLineSegment(sketch, "E193.0.2", {"start": v(7400, 200) * mm, "end": v(7600, 200) * mm});
            skLineSegment(sketch, "E193.0.3", {"start": v(7600, 200) * mm, "end": v(7600, 5800) * mm});
            skLineSegment(sketch, "E194", {"start": v(7400, 5800) * mm, "end": v(7400, 4250) * mm});
            skLineSegment(sketch, "E195", {"start": v(7400, 4250) * mm, "end": v(7600, 4250) * mm});
            skLineSegment(sketch, "E196", {"start": v(7600, 4250) * mm, "end": v(7600, 5800) * mm});
            skLineSegment(sketch, "E197", {"start": v(7400, 4250) * mm, "end": v(7400, 3050) * mm});
            skLineSegment(sketch, "E198", {"start": v(7400, 3050) * mm, "end": v(7600, 3050) * mm});
            skLineSegment(sketch, "E199", {"start": v(7600, 3050) * mm, "end": v(7600, 200) * mm});
            skLineSegment(sketch, "E200", {"start": v(7400, 200) * mm, "end": v(7400, 3050) * mm});
            skSolve(sketch);
        }
        {
            var Q0;
            Q0=makeQuery(id+"F33.imprint","IMPRINT",FACE,{"disambiguationData":[TD([[makeQuery(id+"F33.imprint","IMPRINT",EDGE,{"derivedFrom":sQuery(id+"F33.wireOp",EDGE,"E193.0.0")}),1.0]])]});
            var Q1;
            Q1=makeQuery(id+"F33.imprint","IMPRINT",FACE,{"disambiguationData":[TD([[makeQuery(id+"F33.imprint","IMPRINT",EDGE,{"derivedFrom":sQuery(id+"F33.wireOp",EDGE,"E193.0.2")}),1.0]])]});
            extrude(context, id + "F34", {"entities" : qUnion([Q0, Q1]), "operationType" : NewBodyOperationType.ADD, "depth" : 2800 * mm, "offsetDistance" : 25 * mm});
        }
    });
